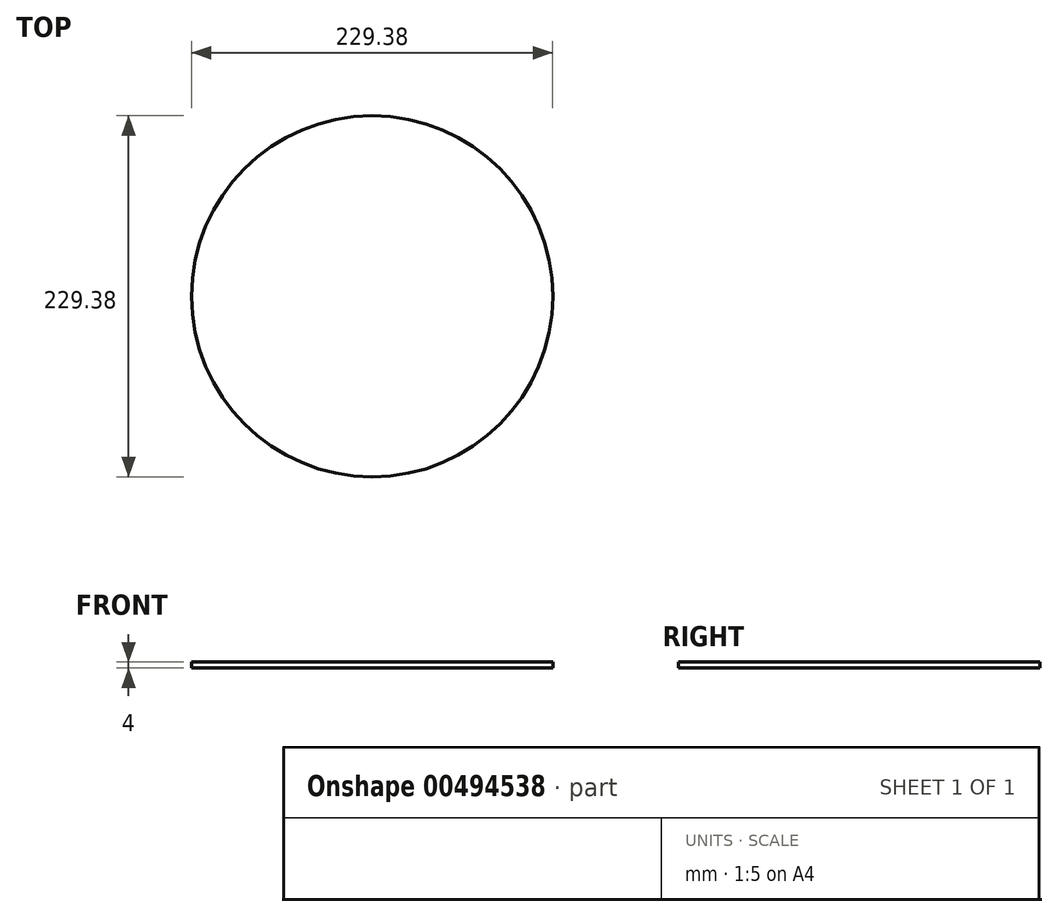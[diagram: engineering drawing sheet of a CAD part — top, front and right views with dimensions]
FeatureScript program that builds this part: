
annotation { "Feature Type Name" : "Feature", "Feature Type Description" : "" }
export const myFeature = defineFeature(function(context is Context, id is Id, definition is map)
    precondition{}
    {
        {
            var Q0;
            Q0=qCreatedBy(makeId("Top.planeOp"),FACE);
            var sketch = newSketch(context, id + "F0", { "sketchPlane" : qUnion([Q0])});
            skCircle(sketch, "E0", {"center": v(0, 0) * mm, "radius": 114.7 * mm});
            skSolve(sketch);
        }
        {
            var Q0;
            Q0=makeQuery(id+"F0.imprint","IMPRINT",FACE,{"disambiguationData":[TD([[makeQuery(id+"F0.imprint","IMPRINT",EDGE,{"derivedFrom":sQuery(id+"F0.wireOp",EDGE,"E0")}),1.0]])]});
            var Q1;
            Q1=sQuery(id+"F0.wireOp",EDGE,"E0");
            extrude(context, id + "F1", {"entities" : qUnion([Q0]), "surfaceEntities" : qUnion([Q1]), "oppositeDirection" : true, "depth" : 4 * mm});
        }
    });
